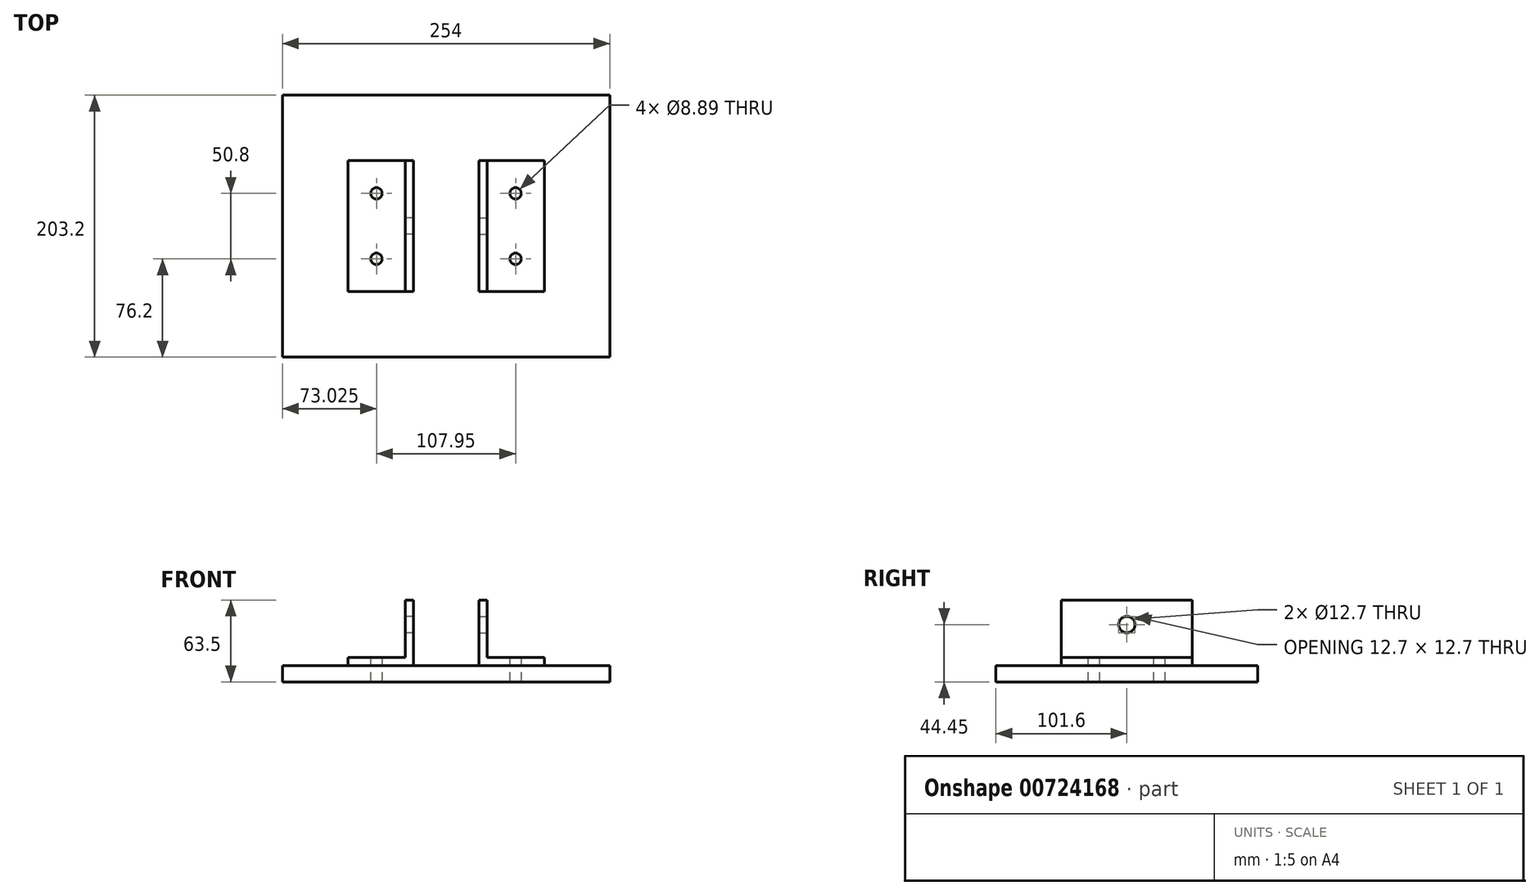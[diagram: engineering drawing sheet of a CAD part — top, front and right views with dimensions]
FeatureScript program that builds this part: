
annotation { "Feature Type Name" : "Feature", "Feature Type Description" : "" }
export const myFeature = defineFeature(function(context is Context, id is Id, definition is map)
    precondition{}
    {
        {
            var Q0;
            Q0=qCreatedBy(makeId("Top.planeOp"),FACE);
            var sketch = newSketch(context, id + "F0", { "sketchPlane" : qUnion([Q0])});
            skLineSegment(sketch, "E0.bottom", {"start": v(127, -101.6) * mm, "end": v(-127, -101.6) * mm});
            skLineSegment(sketch, "E0.top", {"start": v(127, 101.6) * mm, "end": v(-127, 101.6) * mm});
            skLineSegment(sketch, "E0.left", {"start": v(127, -101.6) * mm, "end": v(127, 101.6) * mm});
            skLineSegment(sketch, "E0.right", {"start": v(-127, -101.6) * mm, "end": v(-127, 101.6) * mm});
            skPoint(sketch, "E0.middle", {"position": v(0, 0) * mm});
            skSolve(sketch);
        }
        {
            var Q0;
            Q0 = qSketchRegion(id + "F0", true);
            extrude(context, id + "F1", {"entities" : qUnion([Q0]), "depth" : 12.7 * mm, "offsetDistance" : 25.4 * mm});
        }
        {
            var Q0;
            Q0=makeQuery(id+"F1.opExtrude","CAP_FACE",FACE,{"disambiguationData":[OSD([sQuery(id+"F0.wireOp",EDGE,"E0.bottom"),sQuery(id+"F0.wireOp",EDGE,"E0.top"),sQuery(id+"F0.wireOp",EDGE,"E0.left"),sQuery(id+"F0.wireOp",EDGE,"E0.right")])],"isStart":false});
            var sketch = newSketch(context, id + "F2", { "sketchPlane" : qUnion([Q0])});
            skLineSegment(sketch, "E1", {"start": v(0, 0) * mm, "end": v(-53.97, 0) * mm, "construction": true});
            skLineSegment(sketch, "E2", {"start": v(-53.98, 0) * mm, "end": v(-53.98, 25.4) * mm, "construction": true});
            skLineSegment(sketch, "E3", {"start": v(-53.97, 0) * mm, "end": v(-53.97, -25.4) * mm, "construction": true});
            skCircle(sketch, "E4", {"center": v(-53.98, 25.4) * mm, "radius": 4.45 * mm});
            skCircle(sketch, "E5", {"center": v(-53.97, -25.4) * mm, "radius": 4.45 * mm});
            skLineSegment(sketch, "E6", {"start": v(0, 0) * mm, "end": v(0, 54.06) * mm, "construction": true});
            skCircle(sketch, "E7.MirrorC", {"center": v(53.97, -25.4) * mm, "radius": 4.45 * mm});
            skCircle(sketch, "E8.MirrorC", {"center": v(53.98, 25.4) * mm, "radius": 4.45 * mm});
            skSolve(sketch);
        }
        {
            var Q0;
            Q0 = qSketchRegion(id + "F2", true);
            extrude(context, id + "F3", {"entities" : qUnion([Q0]), "operationType" : NewBodyOperationType.REMOVE, "oppositeDirection" : true, "depth" : 25.4 * mm, "offsetDistance" : 25.4 * mm});
        }
        {
            var Q0;
            Q0=makeQuery(id+"F1.opExtrude","CAP_FACE",FACE,{"disambiguationData":[OSD([sQuery(id+"F0.wireOp",EDGE,"E0.bottom"),sQuery(id+"F0.wireOp",EDGE,"E0.top"),sQuery(id+"F0.wireOp",EDGE,"E0.left"),sQuery(id+"F0.wireOp",EDGE,"E0.right")])],"isStart":false});
            var sketch = newSketch(context, id + "F4", { "sketchPlane" : qUnion([Q0])});
            skLineSegment(sketch, "E9.bottom", {"start": v(25.4, -50.8) * mm, "end": v(-25.4, -50.8) * mm, "construction": true});
            skLineSegment(sketch, "E9.top", {"start": v(25.4, 50.8) * mm, "end": v(-25.4, 50.8) * mm, "construction": true});
            skLineSegment(sketch, "E9.left", {"start": v(25.4, -50.8) * mm, "end": v(25.4, 50.8) * mm, "construction": true});
            skLineSegment(sketch, "E9.right", {"start": v(-25.4, -50.8) * mm, "end": v(-25.4, 50.8) * mm, "construction": true});
            skPoint(sketch, "E9.middle", {"position": v(0, 0) * mm});
            skLineSegment(sketch, "E10.bottom", {"start": v(-25.4, 50.8) * mm, "end": v(-76.2, 50.8) * mm});
            skLineSegment(sketch, "E10.top", {"start": v(-25.4, -50.8) * mm, "end": v(-76.2, -50.8) * mm});
            skLineSegment(sketch, "E10.left", {"start": v(-25.4, 50.8) * mm, "end": v(-25.4, -50.8) * mm});
            skLineSegment(sketch, "E10.right", {"start": v(-76.2, 50.8) * mm, "end": v(-76.2, -50.8) * mm});
            skLineSegment(sketch, "E11", {"start": v(0, 0) * mm, "end": v(0, 65.12) * mm, "construction": true});
            skPoint(sketch, "E11.endSnap0", {"position": v(0, 50.8) * mm});
            skSolve(sketch);
        }
        {
            var Q0;
            Q0 = qSketchRegion(id + "F4", true);
            extrude(context, id + "F5", {"entities" : qUnion([Q0]), "depth" : 6.35 * mm, "offsetDistance" : 25.4 * mm});
        }
        {
            var Q0;
            Q0=makeQuery(id+"F5.opExtrude","CAP_FACE",FACE,{"disambiguationData":[OSD([sQuery(id+"F4.wireOp",EDGE,"E10.bottom"),sQuery(id+"F4.wireOp",EDGE,"E10.top"),sQuery(id+"F4.wireOp",EDGE,"E10.left"),sQuery(id+"F4.wireOp",EDGE,"E10.right")])],"isStart":false});
            var sketch = newSketch(context, id + "F6", { "sketchPlane" : qUnion([Q0])});
            skLineSegment(sketch, "E12.bottom", {"start": v(-25.4, 50.8) * mm, "end": v(-31.75, 50.8) * mm});
            skLineSegment(sketch, "E12.top", {"start": v(-25.4, -50.8) * mm, "end": v(-31.75, -50.8) * mm});
            skLineSegment(sketch, "E12.left", {"start": v(-25.4, 50.8) * mm, "end": v(-25.4, -50.8) * mm});
            skLineSegment(sketch, "E12.right", {"start": v(-31.75, 50.8) * mm, "end": v(-31.75, -50.8) * mm});
            skSolve(sketch);
        }
        {
            var Q0;
            Q0 = qSketchRegion(id + "F6", true);
            extrude(context, id + "F7", {"entities" : qUnion([Q0]), "operationType" : NewBodyOperationType.ADD, "depth" : 44.45 * mm, "offsetDistance" : 25.4 * mm});
        }
        {
            var Q0;
            Q0=makeQuery(id+"F5.opExtrude","CAP_FACE",FACE,{"disambiguationData":[OSD([sQuery(id+"F4.wireOp",EDGE,"E10.bottom"),sQuery(id+"F4.wireOp",EDGE,"E10.top"),sQuery(id+"F4.wireOp",EDGE,"E10.left"),sQuery(id+"F4.wireOp",EDGE,"E10.right")])],"isStart":false});
            var sketch = newSketch(context, id + "F8", { "sketchPlane" : qUnion([Q0])});
            skLineSegment(sketch, "E13", {"start": v(0, 0) * mm, "end": v(-53.98, 0) * mm, "construction": true});
            skLineSegment(sketch, "E14", {"start": v(-53.98, 0) * mm, "end": v(-53.98, 25.4) * mm, "construction": true});
            skLineSegment(sketch, "E15", {"start": v(-53.98, 0) * mm, "end": v(-53.98, -25.4) * mm, "construction": true});
            skCircle(sketch, "E16", {"center": v(-53.98, 25.4) * mm, "radius": 4.45 * mm});
            skCircle(sketch, "E17", {"center": v(-53.98, -25.4) * mm, "radius": 4.45 * mm});
            skSolve(sketch);
        }
        {
            var Q0;
            Q0 = qSketchRegion(id + "F8", true);
            extrude(context, id + "F9", {"entities" : qUnion([Q0]), "operationType" : NewBodyOperationType.REMOVE, "oppositeDirection" : true, "depth" : 25.4 * mm, "offsetDistance" : 25.4 * mm});
        }
        {
            var Q0;
            Q0=makeQuery(id+"F7.opExtrude","SWEPT_FACE",FACE,{"disambiguationData":[OSD([sQuery(id+"F6.wireOp",EDGE,"E12.right")])]});
            var sketch = newSketch(context, id + "F10", { "sketchPlane" : qUnion([Q0])});
            skLineSegment(sketch, "E18", {"start": v(0, 0) * mm, "end": v(0, 44.45) * mm, "construction": true});
            skPoint(sketch, "E18.endSnap0", {"position": v(0, 19.05) * mm});
            skCircle(sketch, "E19", {"center": v(0, 44.45) * mm, "radius": 6.35 * mm});
            skSolve(sketch);
        }
        {
            var Q0;
            Q0 = qSketchRegion(id + "F10", true);
            extrude(context, id + "F11", {"entities" : qUnion([Q0]), "operationType" : NewBodyOperationType.REMOVE, "oppositeDirection" : true, "depth" : 25.4 * mm, "offsetDistance" : 25.4 * mm});
        }
        {
            var Q0;
            Q0=makeQuery(id+"F5.opExtrude","SWEPT_BODY",BODY,{"disambiguationData":[OSD([sQuery(id+"F4.wireOp",EDGE,"E10.bottom"),sQuery(id+"F4.wireOp",EDGE,"E10.top"),sQuery(id+"F4.wireOp",EDGE,"E10.left"),sQuery(id+"F4.wireOp",EDGE,"E10.right")])]});
            var Q1;
            Q1=qCreatedBy(makeId("Right.planeOp"),FACE);
            mirror(context, id + "F12", {"operationType" : NewBodyOperationType.ADD, "entities" : qUnion([Q0]), "mirrorPlane" : qUnion([Q1])});
        }
    });
